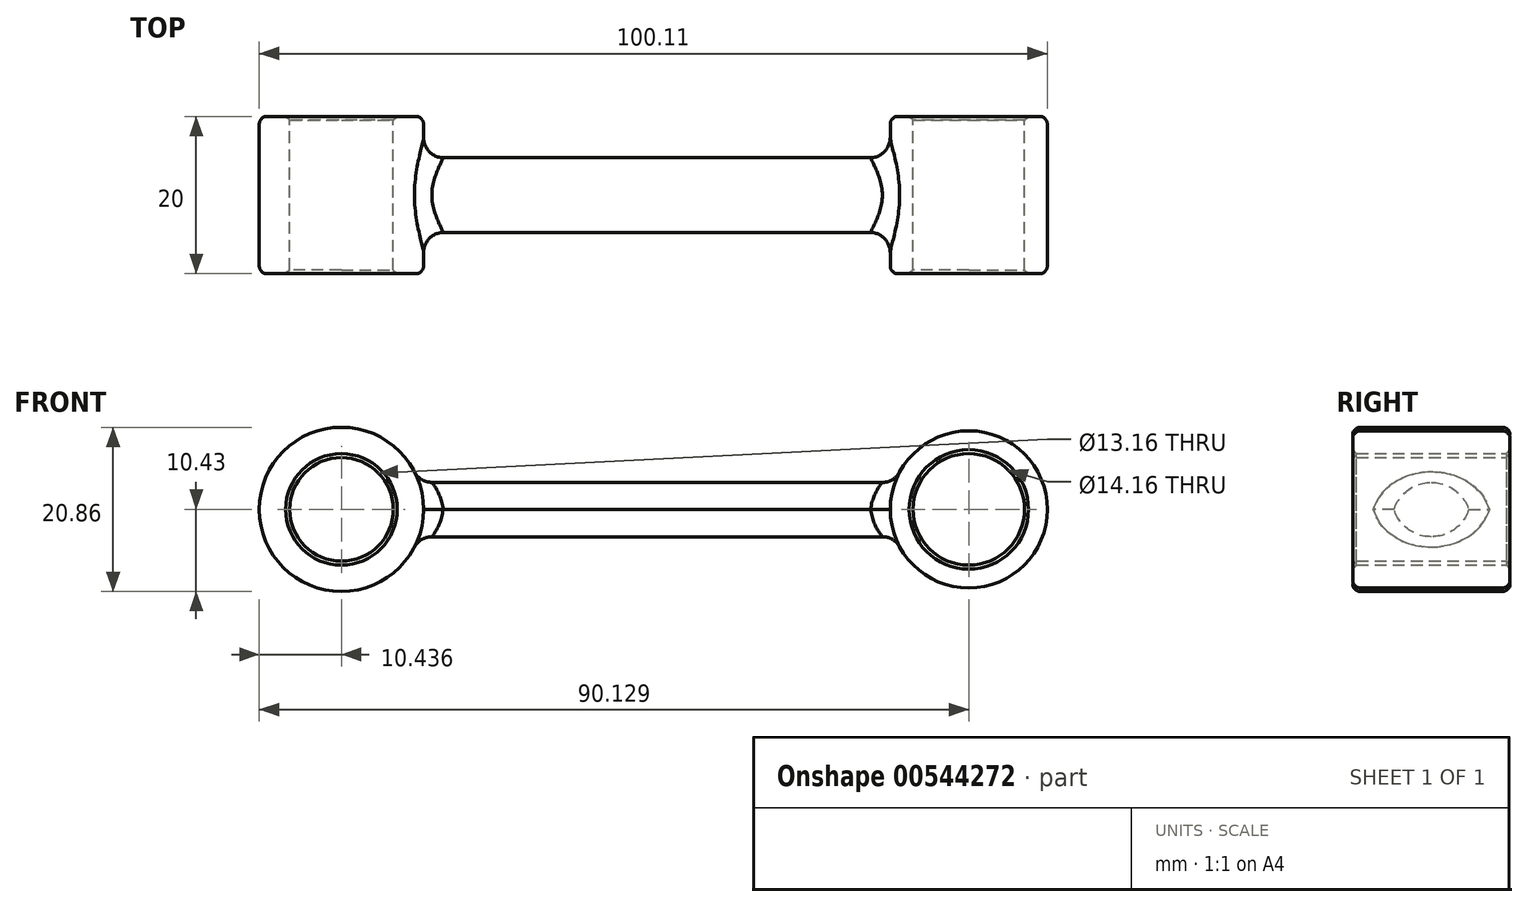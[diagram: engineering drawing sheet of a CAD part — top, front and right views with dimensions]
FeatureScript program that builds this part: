
annotation { "Feature Type Name" : "Feature", "Feature Type Description" : "" }
export const myFeature = defineFeature(function(context is Context, id is Id, definition is map)
    precondition{}
    {
        {
            var Q0;
            Q0=qCreatedBy(makeId("Front.planeOp"),FACE);
            var sketch = newSketch(context, id + "F0", { "sketchPlane" : qUnion([Q0])});
            skCircle(sketch, "E0", {"center": v(-42.51, 0) * mm, "radius": 10.43 * mm});
            skCircle(sketch, "E1", {"center": v(37.18, 0) * mm, "radius": 9.98 * mm});
            skLineSegment(sketch, "E2", {"start": v(-32.68, -3.48) * mm, "end": v(27.83, -3.48) * mm});
            skLineSegment(sketch, "E3", {"start": v(-32.66, 3.43) * mm, "end": v(27.81, 3.43) * mm});
            skCircle(sketch, "E4", {"center": v(-42.51, 0) * mm, "radius": 6.58 * mm});
            skCircle(sketch, "E5", {"center": v(37.18, 0) * mm, "radius": 7.08 * mm});
            skSolve(sketch);
        }
        {
            var Q0;
            Q0=makeQuery(id+"F0.imprint","IMPRINT",FACE,{"disambiguationData":[TD([[makeQuery(id+"F0.imprint","IMPRINT",EDGE,{"derivedFrom":sQuery(id+"F0.wireOp",EDGE,"E4")}),-1.0]])]});
            var Q1;
            Q1=makeQuery(id+"F0.imprint","IMPRINT",FACE,{"disambiguationData":[TD([[makeQuery(id+"F0.imprint","IMPRINT",EDGE,{"derivedFrom":sQuery(id+"F0.wireOp",EDGE,"E5")}),-1.0]])]});
            extrude(context, id + "F1", {"entities" : qUnion([Q0, Q1]), "depth" : 10 * mm, "offsetDistance" : 25 * mm});
        }
        {
            var Q0;
            {var subQ0=sQuery(id+"F0.wireOp",EDGE,"E2");Q0=makeQuery(id+"F0.imprint","IMPRINT",FACE,{"disambiguationData":[TD([[makeQuery(id+"F0.imprint","IMPRINT",EDGE,{"derivedFrom":subQ0}),1.0]])]});}
            extrude(context, id + "F2", {"entities" : qUnion([Q0]), "depth" : 5 * mm, "offsetDistance" : 25 * mm});
        }
        {
            var Q0;
            Q0=makeQuery(id+"F1.opExtrude","SWEPT_BODY",BODY,{"disambiguationData":[OSD([sQuery(id+"F0.wireOp",EDGE,"E0"),sQuery(id+"F0.wireOp",EDGE,"E4")])]});
            var Q1;
            Q1=makeQuery(id+"F2.opExtrude","SWEPT_BODY",BODY,{"disambiguationData":[OSD([sQuery(id+"F0.wireOp",EDGE,"E0"),sQuery(id+"F0.wireOp",EDGE,"E1"),sQuery(id+"F0.wireOp",EDGE,"E2"),sQuery(id+"F0.wireOp",EDGE,"E3")])]});
            var Q2;
            Q2=makeQuery(id+"F1.opExtrude","SWEPT_BODY",BODY,{"disambiguationData":[OSD([sQuery(id+"F0.wireOp",EDGE,"E1"),sQuery(id+"F0.wireOp",EDGE,"E5")])]});
            var Q3;
            Q3 = qSketchRegion(id + "F0", true);
            mirror(context, id + "F3", {"operationType" : NewBodyOperationType.ADD, "entities" : qUnion([Q0, Q1, Q2]), "mirrorPlane" : qUnion([Q3])});
        }
        {
            var Q0;
            Q0=makeQuery(id+"F2.opExtrude","CAP_EDGE",EDGE,{"disambiguationData":[OSD([sQuery(id+"F0.wireOp",EDGE,"E3")])],"isStart":false});
            var Q1;
            Q1=makeQuery(id+"F3.opPattern","COPY",EDGE,{"derivedFrom":makeQuery(id+"F2.opExtrude","CAP_EDGE",EDGE,{"disambiguationData":[OSD([sQuery(id+"F0.wireOp",EDGE,"E3")])],"isStart":false}),"instanceName":"1"});
            var Q2;
            Q2=makeQuery(id+"F2.opExtrude","CAP_EDGE",EDGE,{"disambiguationData":[OSD([sQuery(id+"F0.wireOp",EDGE,"E2")])],"isStart":false});
            var Q3;
            Q3=makeQuery(id+"F3.opPattern","COPY",EDGE,{"derivedFrom":makeQuery(id+"F2.opExtrude","CAP_EDGE",EDGE,{"disambiguationData":[OSD([sQuery(id+"F0.wireOp",EDGE,"E2")])],"isStart":false}),"instanceName":"1"});
            fillet(context, id + "F4", {"entities" : qUnion([Q0, Q1, Q2, Q3]), "radius" : 5 * mm, "tangentPropagation" : true, "allowEdgeOverflow" : false});
        }
        {
            var Q0;
            {var subQ0=makeQuery(id+"F1.opExtrude","SWEPT_FACE",FACE,{"disambiguationData":[OSD([sQuery(id+"F0.wireOp",EDGE,"E0")])]});Q0=makeQuery(id+"F4.opFillet","BLEND_EDGE",EDGE,{"blendedFrom":[makeQuery(id+"F2.opExtrude","CAP_EDGE",EDGE,{"disambiguationData":[OSD([sQuery(id+"F0.wireOp",EDGE,"E3")])],"isStart":false}),makeQuery(id+"F3.boolean.opBoolean","MERGE",FACE,{"derivedFrom":[subQ0,makeQuery(id+"F3.opPattern","COPY",FACE,{"derivedFrom":subQ0,"instanceName":"1"})]})],"blendedInto":[makeQuery(id+"F3.boolean.opBoolean","MERGE",FACE,{"derivedFrom":[subQ0,makeQuery(id+"F3.opPattern","COPY",FACE,{"derivedFrom":subQ0,"instanceName":"1"})]})]});}
            var Q1;
            {var subQ0=makeQuery(id+"F1.opExtrude","SWEPT_FACE",FACE,{"disambiguationData":[OSD([sQuery(id+"F0.wireOp",EDGE,"E0")])]});Q1=makeQuery(id+"F4.opFillet","BLEND_EDGE",EDGE,{"blendedFrom":[makeQuery(id+"F3.opPattern","COPY",EDGE,{"derivedFrom":makeQuery(id+"F2.opExtrude","CAP_EDGE",EDGE,{"disambiguationData":[OSD([sQuery(id+"F0.wireOp",EDGE,"E2")])],"isStart":false}),"instanceName":"1"}),makeQuery(id+"F3.boolean.opBoolean","MERGE",FACE,{"derivedFrom":[subQ0,makeQuery(id+"F3.opPattern","COPY",FACE,{"derivedFrom":subQ0,"instanceName":"1"})]})],"blendedInto":[makeQuery(id+"F3.boolean.opBoolean","MERGE",FACE,{"derivedFrom":[subQ0,makeQuery(id+"F3.opPattern","COPY",FACE,{"derivedFrom":subQ0,"instanceName":"1"})]})]});}
            var Q2;
            {var subQ0=makeQuery(id+"F1.opExtrude","SWEPT_FACE",FACE,{"disambiguationData":[OSD([sQuery(id+"F0.wireOp",EDGE,"E1")])]});Q2=makeQuery(id+"F4.opFillet","BLEND_EDGE",EDGE,{"blendedFrom":[makeQuery(id+"F3.opPattern","COPY",EDGE,{"derivedFrom":makeQuery(id+"F2.opExtrude","CAP_EDGE",EDGE,{"disambiguationData":[OSD([sQuery(id+"F0.wireOp",EDGE,"E2")])],"isStart":false}),"instanceName":"1"}),makeQuery(id+"F3.boolean.opBoolean","MERGE",FACE,{"derivedFrom":[subQ0,makeQuery(id+"F3.opPattern","COPY",FACE,{"derivedFrom":subQ0,"instanceName":"1"})]})],"blendedInto":[makeQuery(id+"F3.boolean.opBoolean","MERGE",FACE,{"derivedFrom":[subQ0,makeQuery(id+"F3.opPattern","COPY",FACE,{"derivedFrom":subQ0,"instanceName":"1"})]})]});}
            var Q3;
            {var subQ0=makeQuery(id+"F1.opExtrude","SWEPT_FACE",FACE,{"disambiguationData":[OSD([sQuery(id+"F0.wireOp",EDGE,"E1")])]});Q3=makeQuery(id+"F4.opFillet","BLEND_EDGE",EDGE,{"blendedFrom":[makeQuery(id+"F2.opExtrude","CAP_EDGE",EDGE,{"disambiguationData":[OSD([sQuery(id+"F0.wireOp",EDGE,"E3")])],"isStart":false}),makeQuery(id+"F3.boolean.opBoolean","MERGE",FACE,{"derivedFrom":[subQ0,makeQuery(id+"F3.opPattern","COPY",FACE,{"derivedFrom":subQ0,"instanceName":"1"})]})],"blendedInto":[makeQuery(id+"F3.boolean.opBoolean","MERGE",FACE,{"derivedFrom":[subQ0,makeQuery(id+"F3.opPattern","COPY",FACE,{"derivedFrom":subQ0,"instanceName":"1"})]})]});}
            fillet(context, id + "F5", {"entities" : qUnion([Q0, Q1, Q2, Q3]), "radius" : 2.5 * mm, "tangentPropagation" : true, "allowEdgeOverflow" : false});
        }
        {
            var Q0;
            Q0=makeQuery(id+"F1.opExtrude","CAP_EDGE",EDGE,{"disambiguationData":[OSD([sQuery(id+"F0.wireOp",EDGE,"E1")])],"isStart":false});
            var Q1;
            Q1=makeQuery(id+"F1.opExtrude","CAP_EDGE",EDGE,{"disambiguationData":[OSD([sQuery(id+"F0.wireOp",EDGE,"E0")])],"isStart":false});
            var Q2;
            Q2=makeQuery(id+"F3.opPattern","COPY",EDGE,{"derivedFrom":makeQuery(id+"F1.opExtrude","CAP_EDGE",EDGE,{"disambiguationData":[OSD([sQuery(id+"F0.wireOp",EDGE,"E0")])],"isStart":false}),"instanceName":"1"});
            var Q3;
            Q3=makeQuery(id+"F3.opPattern","COPY",EDGE,{"derivedFrom":makeQuery(id+"F1.opExtrude","CAP_EDGE",EDGE,{"disambiguationData":[OSD([sQuery(id+"F0.wireOp",EDGE,"E1")])],"isStart":false}),"instanceName":"1"});
            fillet(context, id + "F6", {"entities" : qUnion([Q0, Q1, Q2, Q3]), "radius" : 1 * mm, "tangentPropagation" : true, "allowEdgeOverflow" : false});
        }
        {
            var Q0;
            Q0=makeQuery(id+"F1.opExtrude","CAP_EDGE",EDGE,{"disambiguationData":[OSD([sQuery(id+"F0.wireOp",EDGE,"E5")])],"isStart":false});
            var Q1;
            Q1=makeQuery(id+"F3.opPattern","COPY",EDGE,{"derivedFrom":makeQuery(id+"F1.opExtrude","CAP_EDGE",EDGE,{"disambiguationData":[OSD([sQuery(id+"F0.wireOp",EDGE,"E5")])],"isStart":false}),"instanceName":"1"});
            var Q2;
            Q2=makeQuery(id+"F3.opPattern","COPY",EDGE,{"derivedFrom":makeQuery(id+"F1.opExtrude","CAP_EDGE",EDGE,{"disambiguationData":[OSD([sQuery(id+"F0.wireOp",EDGE,"E4")])],"isStart":false}),"instanceName":"1"});
            var Q3;
            Q3=makeQuery(id+"F1.opExtrude","CAP_EDGE",EDGE,{"disambiguationData":[OSD([sQuery(id+"F0.wireOp",EDGE,"E4")])],"isStart":false});
            chamfer(context, id + "F7", {"entities" : qUnion([Q0, Q1, Q2, Q3]), "width" : 0.5 * mm, "tangentPropagation" : true});
        }
    });
